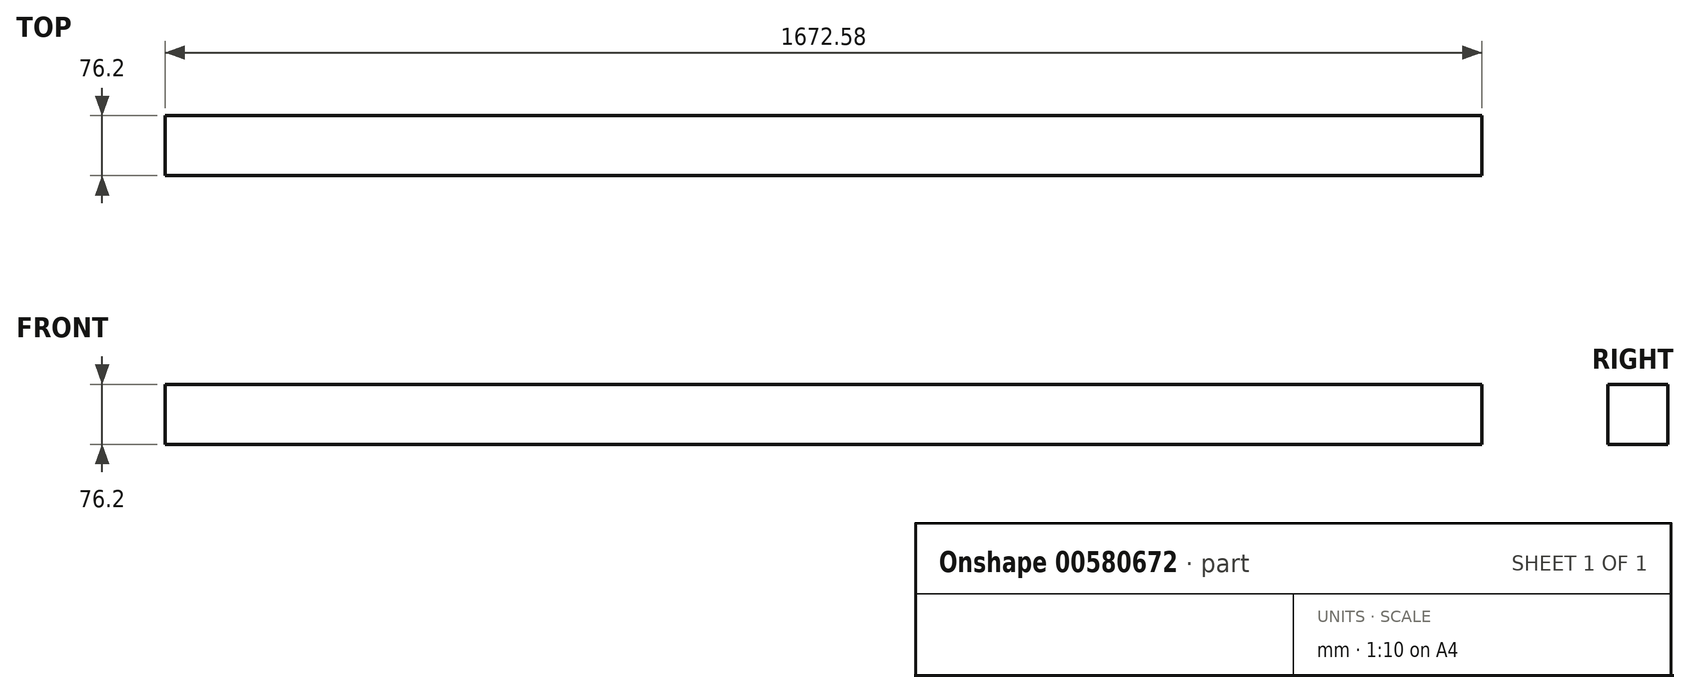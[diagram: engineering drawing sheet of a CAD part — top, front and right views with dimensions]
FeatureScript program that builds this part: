
annotation { "Feature Type Name" : "Feature", "Feature Type Description" : "" }
export const myFeature = defineFeature(function(context is Context, id is Id, definition is map)
    precondition{}
    {
        {
            var Q0;
            Q0=qCreatedBy(makeId("Top.planeOp"),FACE);
            var sketch = newSketch(context, id + "F0", { "sketchPlane" : qUnion([Q0])});
            skLineSegment(sketch, "E0.bottom", {"start": v(836.3, -38.1) * mm, "end": v(-836.3, -38.1) * mm});
            skLineSegment(sketch, "E0.top", {"start": v(836.3, 38.1) * mm, "end": v(-836.3, 38.1) * mm});
            skLineSegment(sketch, "E0.left", {"start": v(836.3, -38.1) * mm, "end": v(836.3, 38.1) * mm});
            skLineSegment(sketch, "E0.right", {"start": v(-836.3, -38.1) * mm, "end": v(-836.3, 38.1) * mm});
            skPoint(sketch, "E0.middle", {"position": v(0, 0) * mm});
            skSolve(sketch);
        }
        {
            var Q0;
            Q0=makeQuery(id+"F0.imprint","IMPRINT",FACE,{"disambiguationData":[TD([[makeQuery(id+"F0.imprint","IMPRINT",EDGE,{"derivedFrom":sQuery(id+"F0.wireOp",EDGE,"E0.bottom")}),-1.0]])]});
            extrude(context, id + "F1", {"entities" : qUnion([Q0]), "depth" : 76.2 * mm, "offsetDistance" : 25.4 * mm});
        }
    });
